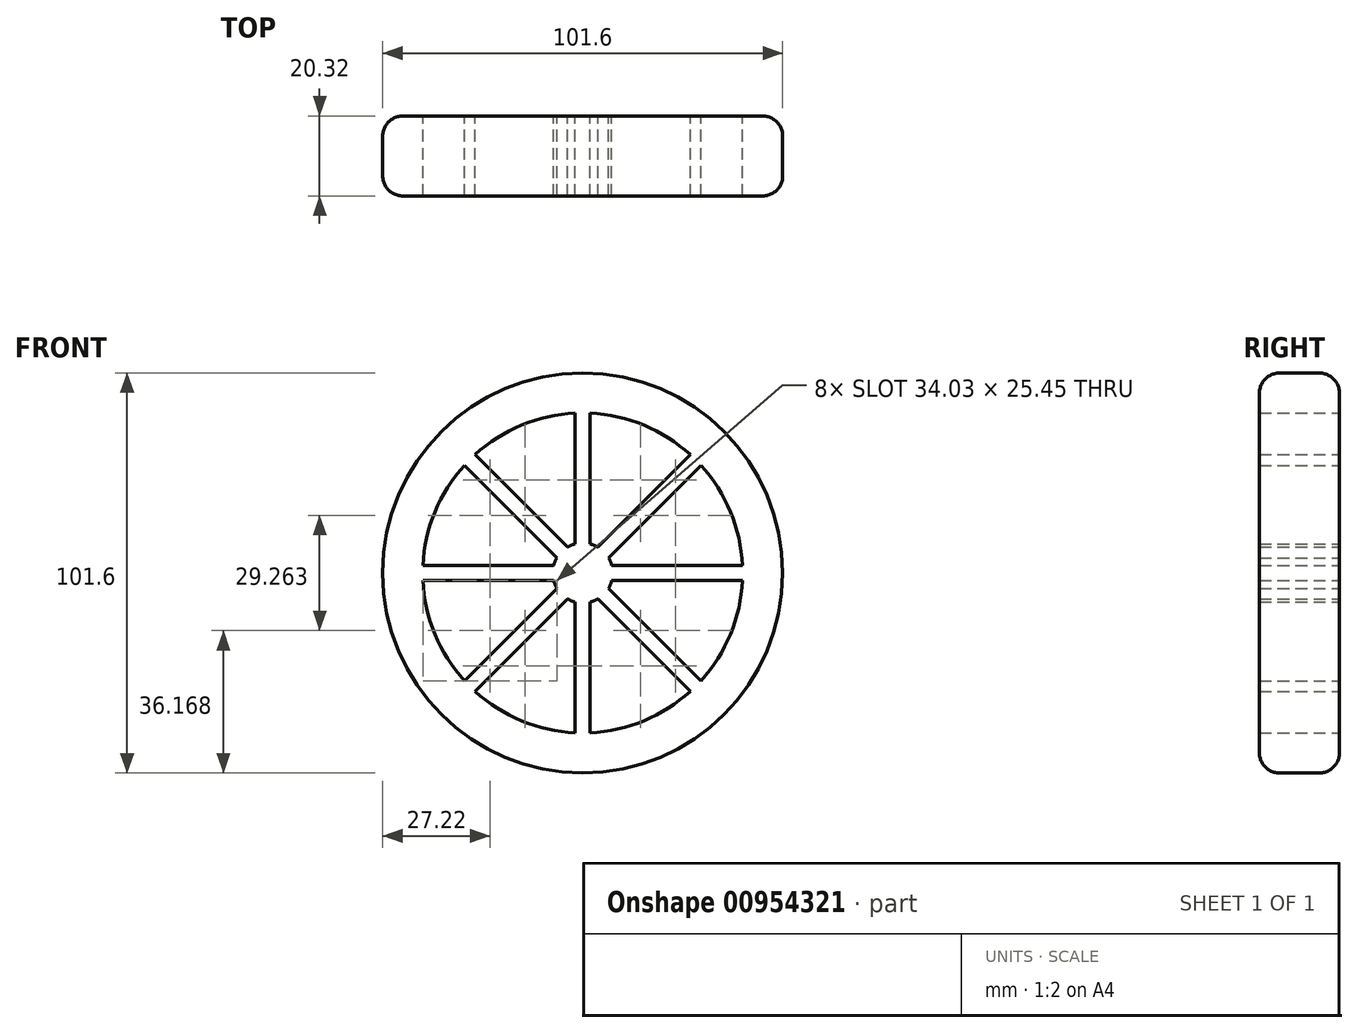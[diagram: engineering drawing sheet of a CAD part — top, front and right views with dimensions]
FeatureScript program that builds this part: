
annotation { "Feature Type Name" : "Feature", "Feature Type Description" : "" }
export const myFeature = defineFeature(function(context is Context, id is Id, definition is map)
    precondition{}
    {
        {
            var Q0;
            Q0=qCreatedBy(makeId("Front.planeOp"),FACE);
            var sketch = newSketch(context, id + "F0", { "sketchPlane" : qUnion([Q0])});
            skCircle(sketch, "E0", {"center": v(0, 0) * mm, "radius": 50.8 * mm});
            skArc(sketch, "E1", {"start": v(-30.05, 27.36) * mm, "mid": v(-37.55, 15.55) * mm, "end": v(-40.6, 1.9) * mm});
            skArc(sketch, "E2", {"start": v(-1.9, 7.38) * mm, "mid": v(-2.92, 7.04) * mm, "end": v(-3.87, 6.56) * mm});
            skLineSegment(sketch, "E3.left", {"start": v(-1.9, 40.6) * mm, "end": v(-1.9, 7.38) * mm});
            skLineSegment(sketch, "E3.right", {"start": v(1.9, 40.6) * mm, "end": v(1.9, 7.38) * mm});
            skPoint(sketch, "E3.middle", {"position": v(0, 23.99) * mm});
            skLineSegment(sketch, "E4.1.0", {"start": v(-27.36, 30.05) * mm, "end": v(-3.87, 6.56) * mm});
            skLineSegment(sketch, "E4.1.1", {"start": v(-30.05, 27.36) * mm, "end": v(-6.56, 3.87) * mm});
            skLineSegment(sketch, "E4.2.0", {"start": v(-40.6, 1.9) * mm, "end": v(-7.38, 1.9) * mm});
            skLineSegment(sketch, "E4.2.1", {"start": v(-40.6, -1.9) * mm, "end": v(-7.38, -1.9) * mm});
            skLineSegment(sketch, "E4.3.0", {"start": v(-30.05, -27.36) * mm, "end": v(-6.56, -3.87) * mm});
            skLineSegment(sketch, "E4.3.1", {"start": v(-27.36, -30.05) * mm, "end": v(-3.87, -6.56) * mm});
            skLineSegment(sketch, "E4.4.0", {"start": v(-1.9, -40.6) * mm, "end": v(-1.9, -7.38) * mm});
            skLineSegment(sketch, "E4.4.1", {"start": v(1.9, -40.6) * mm, "end": v(1.9, -7.38) * mm});
            skLineSegment(sketch, "E4.5.0", {"start": v(27.36, -30.05) * mm, "end": v(3.87, -6.56) * mm});
            skLineSegment(sketch, "E4.5.1", {"start": v(30.05, -27.36) * mm, "end": v(6.56, -3.87) * mm});
            skLineSegment(sketch, "E4.6.0", {"start": v(40.6, -1.9) * mm, "end": v(7.38, -1.9) * mm});
            skLineSegment(sketch, "E4.6.1", {"start": v(40.6, 1.9) * mm, "end": v(7.38, 1.9) * mm});
            skLineSegment(sketch, "E4.7.0", {"start": v(30.05, 27.36) * mm, "end": v(6.56, 3.87) * mm});
            skLineSegment(sketch, "E4.7.1", {"start": v(27.36, 30.05) * mm, "end": v(3.87, 6.56) * mm});
            skArc(sketch, "E5.trimOffspring", {"start": v(-1.9, 40.6) * mm, "mid": v(-15.55, 37.55) * mm, "end": v(-27.36, 30.05) * mm});
            skArc(sketch, "E6.trimOffspring", {"start": v(-6.56, 3.87) * mm, "mid": v(-7.04, 2.92) * mm, "end": v(-7.38, 1.9) * mm});
            skArc(sketch, "E7.trimOffspring", {"start": v(-7.38, -1.9) * mm, "mid": v(-7.04, -2.92) * mm, "end": v(-6.56, -3.87) * mm});
            skArc(sketch, "E8.trimOffspring", {"start": v(-3.87, -6.56) * mm, "mid": v(-2.92, -7.04) * mm, "end": v(-1.9, -7.38) * mm});
            skArc(sketch, "E9.trimOffspring", {"start": v(1.9, -7.38) * mm, "mid": v(2.92, -7.04) * mm, "end": v(3.87, -6.56) * mm});
            skArc(sketch, "E10.trimOffspring", {"start": v(6.56, -3.87) * mm, "mid": v(7.04, -2.92) * mm, "end": v(7.38, -1.9) * mm});
            skArc(sketch, "E11.trimOffspring", {"start": v(7.38, 1.9) * mm, "mid": v(7.04, 2.92) * mm, "end": v(6.56, 3.87) * mm});
            skArc(sketch, "E12.trimOffspring", {"start": v(3.87, 6.56) * mm, "mid": v(2.92, 7.04) * mm, "end": v(1.9, 7.38) * mm});
            skArc(sketch, "E13.trimOffspring", {"start": v(40.6, 1.9) * mm, "mid": v(28.74, 28.74) * mm, "end": v(1.9, 40.6) * mm});
            skArc(sketch, "E14.trimOffspring", {"start": v(30.05, -27.36) * mm, "mid": v(37.55, -15.55) * mm, "end": v(40.6, -1.9) * mm});
            skArc(sketch, "E15.trimOffspring", {"start": v(1.9, -40.6) * mm, "mid": v(15.55, -37.55) * mm, "end": v(27.36, -30.05) * mm});
            skArc(sketch, "E16.trimOffspring", {"start": v(-27.36, -30.05) * mm, "mid": v(-15.55, -37.55) * mm, "end": v(-1.9, -40.6) * mm});
            skArc(sketch, "E17.trimOffspring", {"start": v(-40.6, -1.9) * mm, "mid": v(-37.55, -15.55) * mm, "end": v(-30.05, -27.36) * mm});
            skSolve(sketch);
        }
        {
            var Q0;
            Q0=makeQuery(id+"F0.imprint","IMPRINT",FACE,{"disambiguationData":[TD([[makeQuery(id+"F0.imprint","IMPRINT",EDGE,{"derivedFrom":sQuery(id+"F0.wireOp",EDGE,"E0")}),1.0]])]});
            extrude(context, id + "F1", {"entities" : qUnion([Q0]), "depth" : 20.32 * mm, "offsetDistance" : 25.4 * mm});
        }
        {
            var Q0;
            Q0=makeQuery(id+"F1.opExtrude","CAP_EDGE",EDGE,{"disambiguationData":[OSD([sQuery(id+"F0.wireOp",EDGE,"E0")])],"isStart":false});
            var Q1;
            Q1=makeQuery(id+"F1.opExtrude","CAP_EDGE",EDGE,{"disambiguationData":[OSD([sQuery(id+"F0.wireOp",EDGE,"E0")])],"isStart":true});
            fillet(context, id + "F2", {"entities" : qUnion([Q0, Q1]), "radius" : 5.08 * mm, "tangentPropagation" : true, "allowEdgeOverflow" : false});
        }
    });
